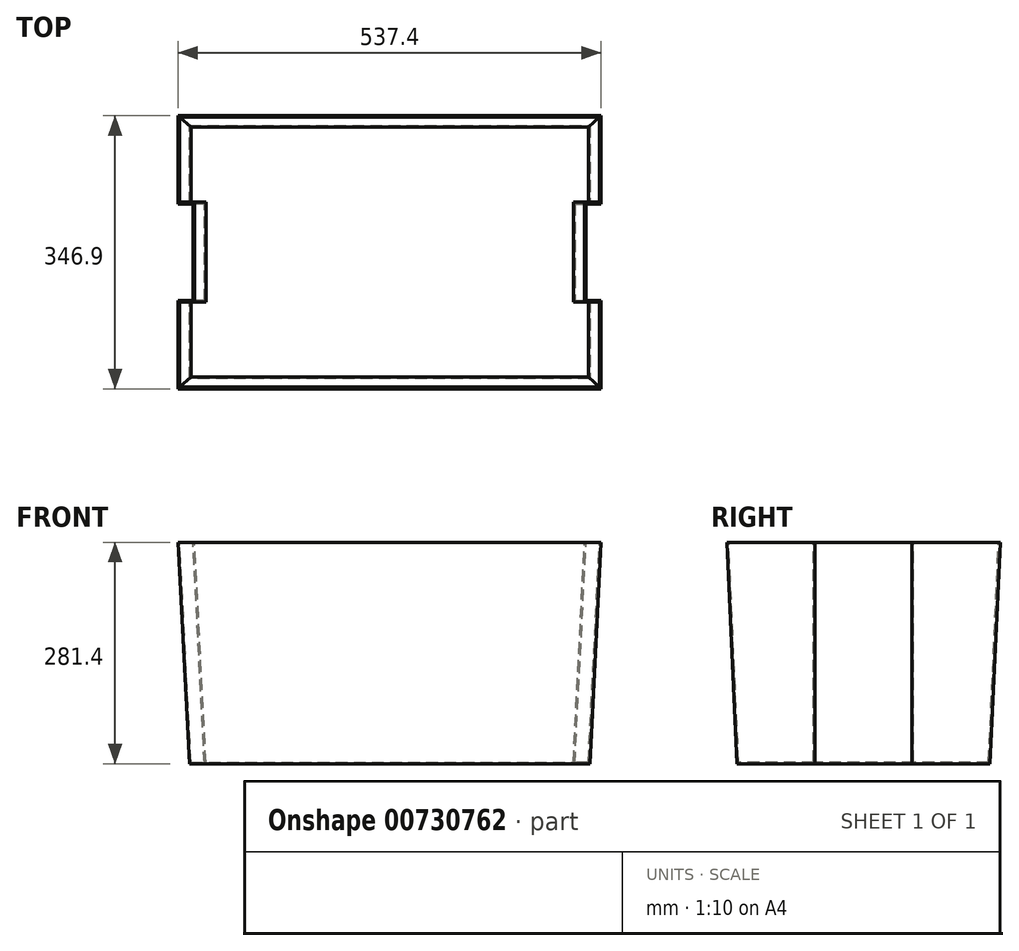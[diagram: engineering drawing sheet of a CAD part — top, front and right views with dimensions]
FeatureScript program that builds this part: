
annotation { "Feature Type Name" : "Feature", "Feature Type Description" : "" }
export const myFeature = defineFeature(function(context is Context, id is Id, definition is map)
    precondition{}
    {
        {
            var Q0;
            Q0=qCreatedBy(makeId("Top.planeOp"),FACE);
            var sketch = newSketch(context, id + "F0", { "sketchPlane" : qUnion([Q0])});
            skLineSegment(sketch, "E0.bottom", {"start": v(-233.36, 158.75) * mm, "end": v(233.36, 158.75) * mm, "construction": true});
            skLineSegment(sketch, "E0.top", {"start": v(-233.36, -158.75) * mm, "end": v(233.36, -158.75) * mm, "construction": true});
            skLineSegment(sketch, "E0.left", {"start": v(-233.36, 158.75) * mm, "end": v(-233.36, -158.75) * mm, "construction": true});
            skLineSegment(sketch, "E0.right", {"start": v(233.36, 158.75) * mm, "end": v(233.36, -158.75) * mm, "construction": true});
            skPoint(sketch, "E0.middle", {"position": v(0, 0) * mm});
            skLineSegment(sketch, "E1", {"start": v(-252.41, 158.75) * mm, "end": v(-252.41, -158.75) * mm, "construction": true});
            skLineSegment(sketch, "E2", {"start": v(252.41, 158.75) * mm, "end": v(252.41, -158.75) * mm, "construction": true});
            skLineSegment(sketch, "E3", {"start": v(-252.41, 158.75) * mm, "end": v(252.41, 158.75) * mm});
            skLineSegment(sketch, "E4", {"start": v(252.41, 158.75) * mm, "end": v(252.41, 63.5) * mm});
            skLineSegment(sketch, "E5", {"start": v(252.41, 63.5) * mm, "end": v(233.36, 63.5) * mm});
            skLineSegment(sketch, "E6", {"start": v(233.36, 63.5) * mm, "end": v(233.36, -63.5) * mm});
            skLineSegment(sketch, "E7", {"start": v(233.36, -63.5) * mm, "end": v(252.41, -63.5) * mm});
            skLineSegment(sketch, "E8", {"start": v(252.41, -63.5) * mm, "end": v(252.41, -158.75) * mm});
            skLineSegment(sketch, "E9", {"start": v(252.41, -158.75) * mm, "end": v(-252.41, -158.75) * mm});
            skLineSegment(sketch, "E10", {"start": v(-252.41, -158.75) * mm, "end": v(-252.41, -63.5) * mm});
            skLineSegment(sketch, "E11", {"start": v(-252.41, -63.5) * mm, "end": v(-233.36, -63.5) * mm});
            skLineSegment(sketch, "E12", {"start": v(-233.36, -63.5) * mm, "end": v(-233.36, 63.5) * mm});
            skLineSegment(sketch, "E13", {"start": v(-233.36, 63.5) * mm, "end": v(-252.41, 63.5) * mm});
            skLineSegment(sketch, "E14", {"start": v(-252.41, 63.5) * mm, "end": v(-252.41, 158.75) * mm});
            skLineSegment(sketch, "E15", {"start": v(-418.92, 0) * mm, "end": v(377.31, 0) * mm, "construction": true});
            skPoint(sketch, "E15.endSnap0", {"position": v(-233.36, 0) * mm});
            skSolve(sketch);
        }
        {
            var Q0;
            Q0=qCreatedBy(makeId("Top.planeOp"),FACE);
            cPlane(context, id + "F1", {"entities" : qUnion([Q0]), "cplaneType" : CPlaneType.OFFSET, "offset" : 279.4 * mm, "width" : 152.4 * mm, "height" : 152.4 * mm});
        }
        {
            var Q0;
            Q0=qCreatedBy(id+"F1.planeOp",FACE);
            var sketch = newSketch(context, id + "F2", { "sketchPlane" : qUnion([Q0])});
            skLineSegment(sketch, "E16.bottom", {"start": v(-247.65, 171.45) * mm, "end": v(247.65, 171.45) * mm, "construction": true});
            skLineSegment(sketch, "E16.top", {"start": v(-247.65, -171.45) * mm, "end": v(247.65, -171.45) * mm, "construction": true});
            skLineSegment(sketch, "E16.left", {"start": v(-247.65, 171.45) * mm, "end": v(-247.65, -171.45) * mm, "construction": true});
            skLineSegment(sketch, "E16.right", {"start": v(247.65, 171.45) * mm, "end": v(247.65, -171.45) * mm, "construction": true});
            skPoint(sketch, "E16.middle", {"position": v(0, 0) * mm});
            skLineSegment(sketch, "E17", {"start": v(-266.7, 171.45) * mm, "end": v(-266.7, -171.45) * mm, "construction": true});
            skLineSegment(sketch, "E18", {"start": v(266.7, 171.45) * mm, "end": v(266.7, -171.45) * mm, "construction": true});
            skLineSegment(sketch, "E19", {"start": v(-266.7, 171.45) * mm, "end": v(266.7, 171.45) * mm});
            skLineSegment(sketch, "E20", {"start": v(266.7, 171.45) * mm, "end": v(266.7, 63.5) * mm});
            skLineSegment(sketch, "E21", {"start": v(266.7, 63.5) * mm, "end": v(247.65, 63.5) * mm});
            skLineSegment(sketch, "E22", {"start": v(247.65, 63.5) * mm, "end": v(247.65, -63.5) * mm});
            skLineSegment(sketch, "E23", {"start": v(247.65, -63.5) * mm, "end": v(266.7, -63.5) * mm});
            skLineSegment(sketch, "E24", {"start": v(266.7, -63.5) * mm, "end": v(266.7, -171.45) * mm});
            skLineSegment(sketch, "E25", {"start": v(266.7, -171.45) * mm, "end": v(-266.7, -171.45) * mm});
            skLineSegment(sketch, "E26", {"start": v(-266.7, -171.45) * mm, "end": v(-266.7, -63.5) * mm});
            skLineSegment(sketch, "E27", {"start": v(-266.7, -63.5) * mm, "end": v(-247.65, -63.5) * mm});
            skLineSegment(sketch, "E28", {"start": v(-247.65, -63.5) * mm, "end": v(-247.65, 63.5) * mm});
            skLineSegment(sketch, "E29", {"start": v(-247.65, 63.5) * mm, "end": v(-266.7, 63.5) * mm});
            skLineSegment(sketch, "E30", {"start": v(-266.7, 63.5) * mm, "end": v(-266.7, 171.45) * mm});
            skLineSegment(sketch, "E31", {"start": v(-406.82, 0) * mm, "end": v(389.42, 0) * mm, "construction": true});
            skPoint(sketch, "E31.endSnap0", {"position": v(-247.65, 0) * mm});
            skSolve(sketch);
        }
        {
            var Q0;
            Q0=makeQuery(id+"F0.imprint","IMPRINT",FACE,{"disambiguationData":[TD([[makeQuery(id+"F0.imprint","IMPRINT",EDGE,{"derivedFrom":sQuery(id+"F0.wireOp",EDGE,"E3")}),-1.0]])]});
            var Q1;
            Q1=makeQuery(id+"F2.imprint","IMPRINT",FACE,{"disambiguationData":[TD([[makeQuery(id+"F2.imprint","IMPRINT",EDGE,{"derivedFrom":sQuery(id+"F2.wireOp",EDGE,"E19")}),-1.0]])]});
            loft(context, id + "F3", {"sheetProfilesArray" : [{ "sheetProfileEntities" : qUnion([Q0]) }, { "sheetProfileEntities" : qUnion([Q1]) }]});
        }
        {
            var Q0;
            Q0=makeQuery(id+"F3.opLoft","CAP_FACE",FACE,{"disambiguationData":[OSD([makeQuery(id+"F2.imprint","IMPRINT",FACE,{"disambiguationData":[TD([[makeQuery(id+"F2.imprint","IMPRINT",EDGE,{"derivedFrom":sQuery(id+"F2.wireOp",EDGE,"E19")}),-1.0]])]})])],"isStart":true});
            shell(context, id + "F4", {"entities" : qUnion([Q0]), "thickness" : 2 * mm, "oppositeDirection" : true});
        }
    });
